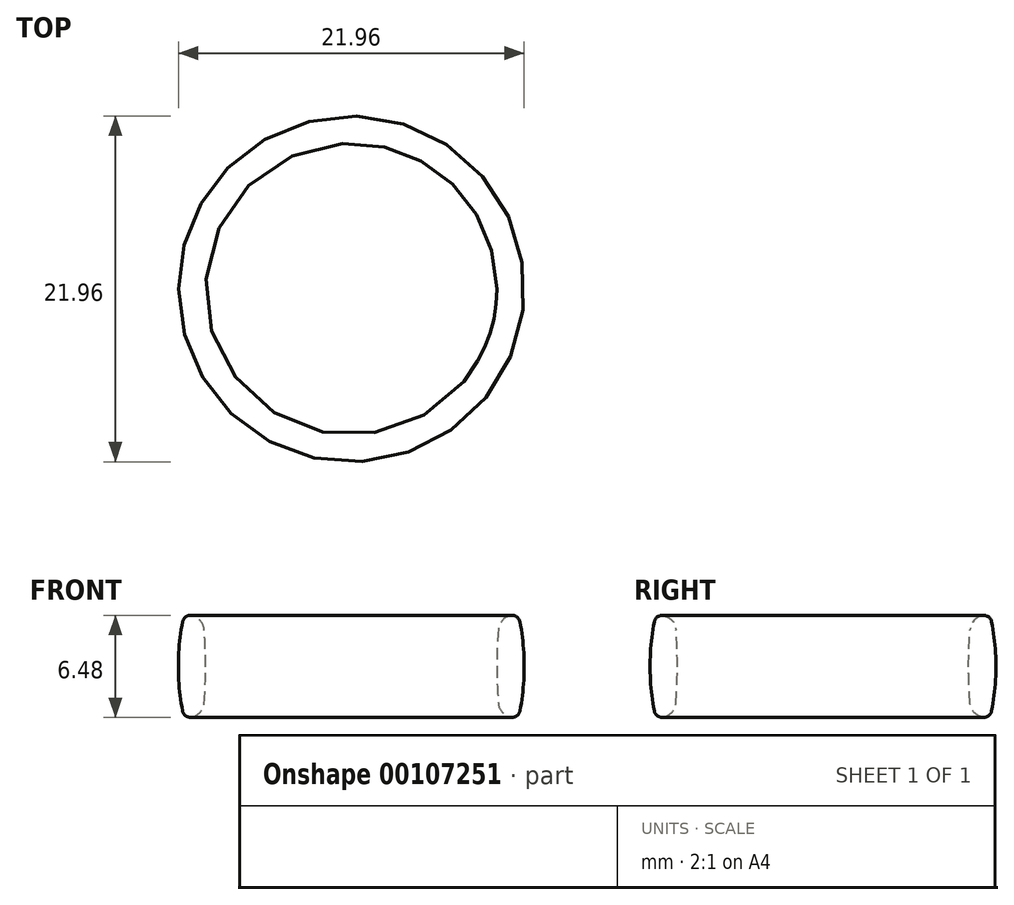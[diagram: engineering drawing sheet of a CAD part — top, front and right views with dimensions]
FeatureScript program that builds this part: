
annotation { "Feature Type Name" : "Feature", "Feature Type Description" : "" }
export const myFeature = defineFeature(function(context is Context, id is Id, definition is map)
    precondition{}
    {
        {
            var Q0;
            Q0=qCreatedBy(makeId("Top.planeOp"),FACE);
            var sketch = newSketch(context, id + "F0", { "sketchPlane" : qUnion([Q0])});
            skEllipse(sketch, "E0", {"center": v(0, 0) * mm, "majorRadius": 9.1 * mm, "minorRadius": 9.1 * mm, "majorAxis": v(1, 0)});
            skSolve(sketch);
        }
        {
            var Q0;
            Q0=qCreatedBy(makeId("Front.planeOp"),FACE);
            var sketch = newSketch(context, id + "F1", { "sketchPlane" : qUnion([Q0])});
            skLineSegment(sketch, "E1.bottom", {"start": v(9.43, 3.25) * mm, "end": v(10.63, 3.25) * mm});
            skLineSegment(sketch, "E1.top", {"start": v(9.43, -3.25) * mm, "end": v(10.63, -3.25) * mm});
            skLineSegment(sketch, "E1.left", {"start": v(9.43, 3.25) * mm, "end": v(9.43, -3.25) * mm, "construction": true});
            skLineSegment(sketch, "E1.right", {"start": v(10.63, 3.25) * mm, "end": v(10.63, -3.25) * mm, "construction": true});
            skLineSegment(sketch, "E2", {"start": v(0, 0) * mm, "end": v(9.25, 0) * mm, "construction": true});
            skArc(sketch, "E3", {"start": v(9.43, 3.25) * mm, "mid": v(9.25, 0) * mm, "end": v(9.43, -3.25) * mm});
            skArc(sketch, "E4", {"start": v(10.63, -3.25) * mm, "mid": v(10.98, 0) * mm, "end": v(10.63, 3.25) * mm});
            skSolve(sketch);
        }
        {
            var Q0;
            Q0=makeQuery(id+"F1.imprint","IMPRINT",FACE,{"disambiguationData":[TD([[makeQuery(id+"F1.imprint","IMPRINT",EDGE,{"derivedFrom":sQuery(id+"F1.wireOp",EDGE,"E1.bottom")}),-1.0]])]});
            var Q1;
            Q1=qConstructionFilter(qBodyType(qCreatedBy(id+"F0",EDGE),BodyType.WIRE),ConstructionObject.NO);
            sweep(context, id + "F2", {"profiles" : qUnion([Q0]), "path" : qUnion([Q1])});
        }
        {
            var Q0;
            Q0=makeQuery(id+"F2.opSweep","SWEPT_EDGE",EDGE,{"disambiguationData":[OSD([sQuery(id+"F0.wireOp",EDGE,"E0"),sQuery(id+"F1.wireOp",EDGE,"E1.bottom"),sQuery(id+"F1.wireOp",EDGE,"E3")])]});
            var Q1;
            Q1=makeQuery(id+"F2.opSweep","SWEPT_EDGE",EDGE,{"disambiguationData":[OSD([sQuery(id+"F0.wireOp",EDGE,"E0"),sQuery(id+"F1.wireOp",EDGE,"E1.top"),sQuery(id+"F1.wireOp",EDGE,"E3")])]});
            fillet(context, id + "F3", {"entities" : qUnion([Q0, Q1]), "radius" : 1 * mm, "tangentPropagation" : true, "allowEdgeOverflow" : false});
        }
        {
            var Q0;
            Q0=makeQuery(id+"F2.opSweep","SWEPT_EDGE",EDGE,{"disambiguationData":[OSD([sQuery(id+"F0.wireOp",EDGE,"E0"),sQuery(id+"F1.wireOp",EDGE,"E1.bottom"),sQuery(id+"F1.wireOp",EDGE,"E4")])]});
            var Q1;
            Q1=makeQuery(id+"F2.opSweep","SWEPT_EDGE",EDGE,{"disambiguationData":[OSD([sQuery(id+"F0.wireOp",EDGE,"E0"),sQuery(id+"F1.wireOp",EDGE,"E1.top"),sQuery(id+"F1.wireOp",EDGE,"E4")])]});
            fillet(context, id + "F4", {"entities" : qUnion([Q0, Q1]), "radius" : 0.5 * mm, "tangentPropagation" : true, "allowEdgeOverflow" : false});
        }
    });
